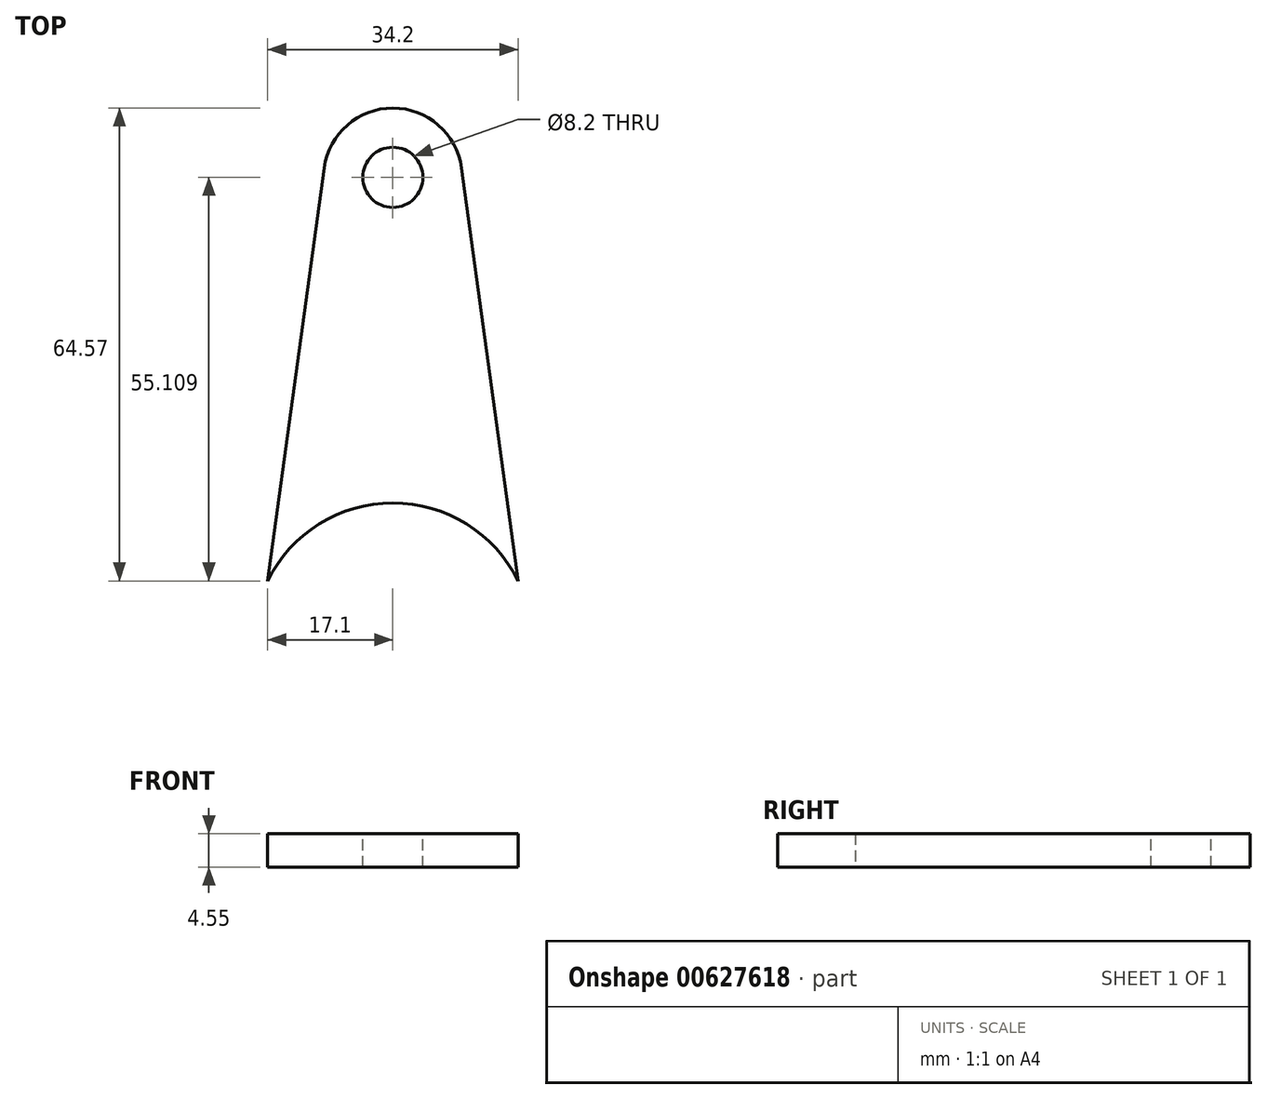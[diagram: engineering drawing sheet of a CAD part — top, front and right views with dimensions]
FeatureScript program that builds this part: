
annotation { "Feature Type Name" : "Feature", "Feature Type Description" : "" }
export const myFeature = defineFeature(function(context is Context, id is Id, definition is map)
    precondition{}
    {
        {
            var Q0;
            Q0=qCreatedBy(makeId("Top.planeOp"),FACE);
            var sketch = newSketch(context, id + "F0", { "sketchPlane" : qUnion([Q0])});
            skLineSegment(sketch, "E0", {"start": v(0, -49.37) * mm, "end": v(0, 65.55) * mm, "construction": true});
            skArc(sketch, "E1", {"start": v(0, 29.22) * mm, "mid": v(-6.22, 26.89) * mm, "end": v(-9.37, 21.04) * mm});
            skArc(sketch, "E2", {"start": v(0, -24.7) * mm, "mid": v(-10.08, -27.57) * mm, "end": v(-17.1, -35.35) * mm});
            skLineSegment(sketch, "E3", {"start": v(-17.1, -35.35) * mm, "end": v(-9.37, 21.04) * mm});
            skArc(sketch, "E4.MirrorCS", {"start": v(0, 29.22) * mm, "mid": v(6.22, 26.89) * mm, "end": v(9.37, 21.04) * mm});
            skLineSegment(sketch, "E5.MirrorCS", {"start": v(17.1, -35.35) * mm, "end": v(9.37, 21.04) * mm});
            skArc(sketch, "E6.MirrorCS", {"start": v(0, -24.7) * mm, "mid": v(10.08, -27.57) * mm, "end": v(17.1, -35.35) * mm});
            skLineSegment(sketch, "E7", {"start": v(17.1, -35.35) * mm, "end": v(17.1, -35.35) * mm});
            skSolve(sketch);
        }
        {
            var Q0;
            Q0=qSketchRegion(id+"F0",true);
            extrude(context, id + "F1", {"entities" : qUnion([Q0]), "depth" : 4.55 * mm, "offsetDistance" : 25.4 * mm});
        }
        {
            var Q0;
            Q0=makeQuery(id+"F1.opExtrude","CAP_FACE",FACE,{"disambiguationData":[OSD([sQuery(id+"F0.wireOp",EDGE,"E1"),sQuery(id+"F0.wireOp",EDGE,"E2"),sQuery(id+"F0.wireOp",EDGE,"E3"),sQuery(id+"F0.wireOp",EDGE,"E4.MirrorCS"),sQuery(id+"F0.wireOp",EDGE,"E5.MirrorCS"),sQuery(id+"F0.wireOp",EDGE,"E6.MirrorCS"),sQuery(id+"F0.wireOp",EDGE,"rgRoUT8c-bVL2-FPYU-7MTc-vp1h9EsBAV6d"),sQuery(id+"F0.wireOp",EDGE,"05189ca0-4bbf-4e7c-aff5-e242d629c5390.MirrorCS")])],"isStart":false});
            var sketch = newSketch(context, id + "F2", { "sketchPlane" : qUnion([Q0])});
            skPoint(sketch, "E8", {"position": v(0, 19.76) * mm});
            skSolve(sketch);
        }
        {
            var Q0;
            Q0=sQuery(id+"F2.wireOp",VERTEX,"E8");
            var Q1;
            Q1=makeQuery(id+"F1.opExtrude","SWEPT_BODY",BODY,{"disambiguationData":[OSD([sQuery(id+"F0.wireOp",EDGE,"E1"),sQuery(id+"F0.wireOp",EDGE,"E2"),sQuery(id+"F0.wireOp",EDGE,"E3"),sQuery(id+"F0.wireOp",EDGE,"E4.MirrorCS"),sQuery(id+"F0.wireOp",EDGE,"E5.MirrorCS"),sQuery(id+"F0.wireOp",EDGE,"E6.MirrorCS"),sQuery(id+"F0.wireOp",EDGE,"rgRoUT8c-bVL2-FPYU-7MTc-vp1h9EsBAV6d"),sQuery(id+"F0.wireOp",EDGE,"05189ca0-4bbf-4e7c-aff5-e242d629c5390.MirrorCS")])]});
            hole(context, id + "F3", {"style" : HoleStyle.SIMPLE, "endStyle" : HoleEndStyle.THROUGH, "standardTappedOrClearance" : lookupTablePath({ "standard" : "ANSI", "fit" : "Close", "size" : "5/16", "type" : "Clearance" }), "standardBlindInLast" : lookupTablePath({ "fit" : "Close", "standard" : "ANSI", "size" : "5/16", "type" : "Clearance" }), "holeDiameter" : 8.2 * mm, "isTappedThrough" : true, "tappedDepth" : 12.7 * mm, "tapClearance" : 3, "locations" : qUnion([Q0]), "scope" : qUnion([Q1]), "majorDiameter" : 6.35 * mm});
        }
    });
